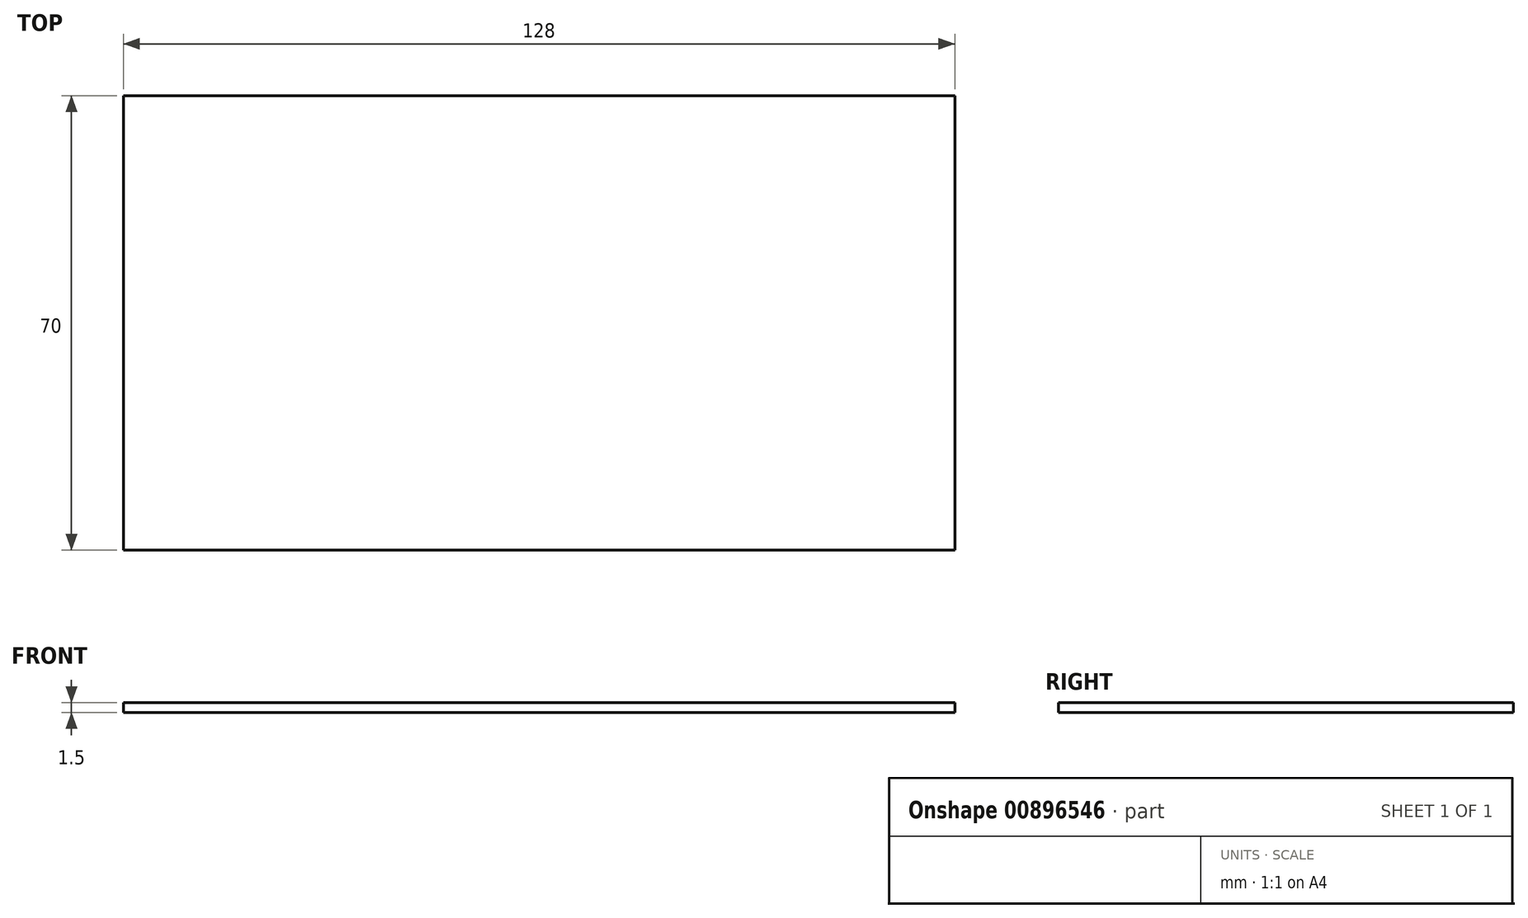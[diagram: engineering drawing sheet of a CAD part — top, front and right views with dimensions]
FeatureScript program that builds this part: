
annotation { "Feature Type Name" : "Feature", "Feature Type Description" : "" }
export const myFeature = defineFeature(function(context is Context, id is Id, definition is map)
    precondition{}
    {
        {
            var Q0;
            Q0=qCreatedBy(makeId("Top.planeOp"),FACE);
            var sketch = newSketch(context, id + "F0", { "sketchPlane" : qUnion([Q0])});
            skLineSegment(sketch, "E0.bottom", {"start": v(0, 0) * mm, "end": v(128, 0) * mm});
            skLineSegment(sketch, "E0.top", {"start": v(0, 70) * mm, "end": v(128, 70) * mm});
            skLineSegment(sketch, "E0.left", {"start": v(0, 0) * mm, "end": v(0, 70) * mm});
            skLineSegment(sketch, "E0.right", {"start": v(128, 0) * mm, "end": v(128, 70) * mm});
            skSolve(sketch);
        }
        {
            var Q0;
            Q0 = qSketchRegion(id + "F0", true);
            extrude(context, id + "F1", {"entities" : qUnion([Q0]), "depth" : 1.5 * mm, "offsetDistance" : 25 * mm});
        }
    });
